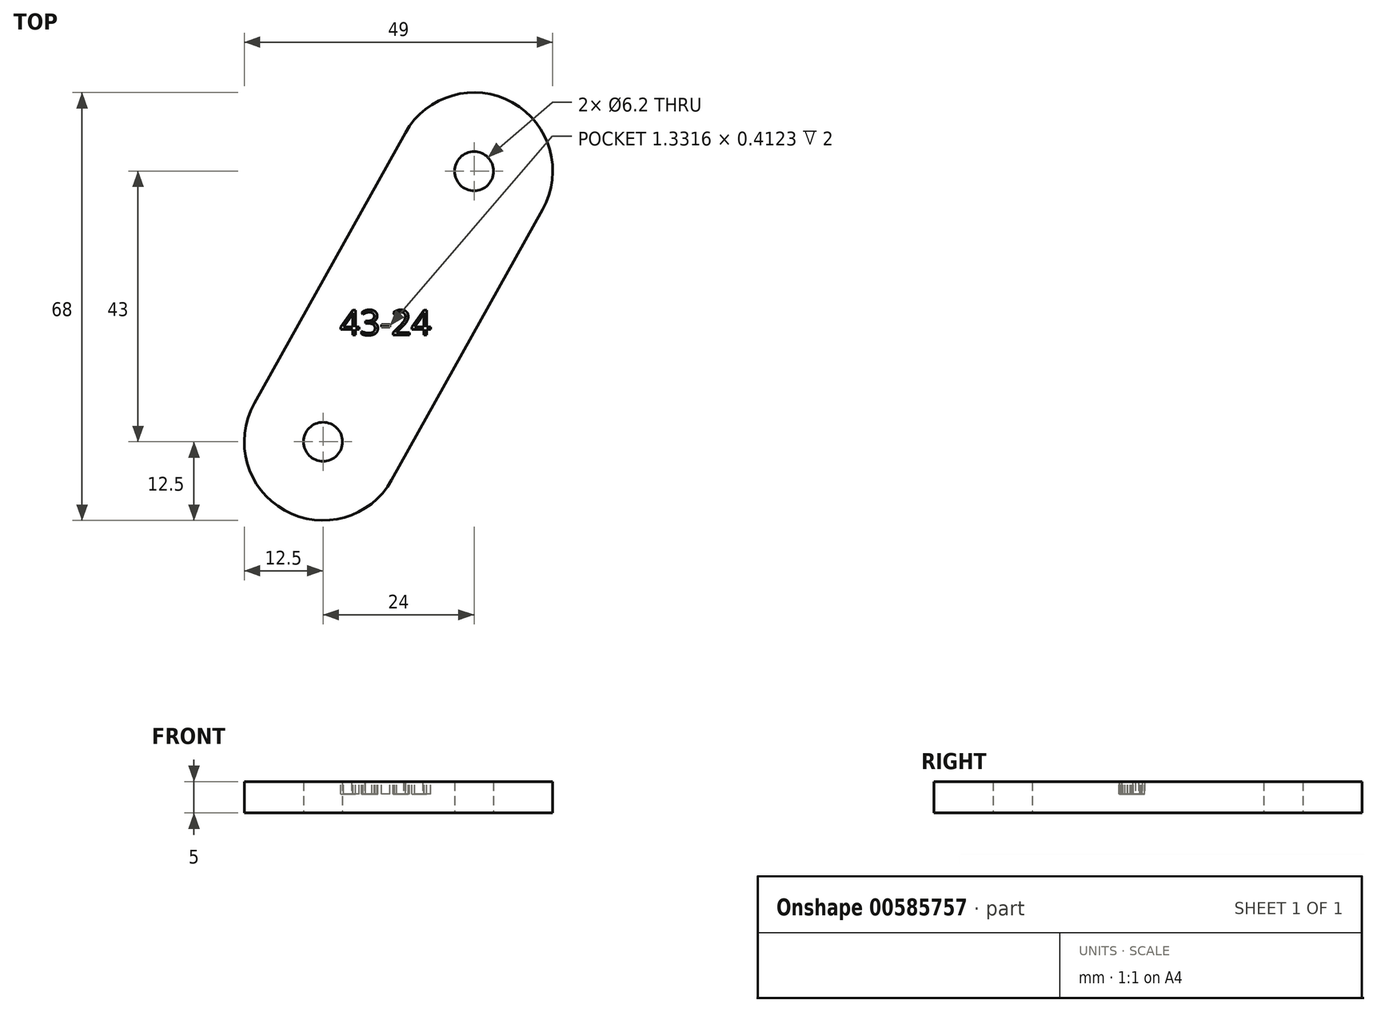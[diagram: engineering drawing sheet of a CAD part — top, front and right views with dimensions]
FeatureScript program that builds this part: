
annotation { "Feature Type Name" : "Feature", "Feature Type Description" : "" }
export const myFeature = defineFeature(function(context is Context, id is Id, definition is map)
    precondition{}
    {
        {
            assignVariable(context, id + "F0", {"name" : "Epaisseur", "anyValue" : 5});
        }
        {
            var Q0;
            Q0=qCreatedBy(makeId("Top.planeOp"),FACE);
            var sketch = newSketch(context, id + "F1", { "sketchPlane" : qUnion([Q0])});
            skArc(sketch, "E0", {"start": v(-10.91, 6.1) * mm, "mid": v(-6.1, -10.91) * mm, "end": v(10.91, -6.1) * mm});
            skArc(sketch, "E1", {"start": v(34.91, 36.9) * mm, "mid": v(30.1, 53.91) * mm, "end": v(13.09, 49.1) * mm});
            skCircle(sketch, "E2", {"center": v(0, 0) * mm, "radius": 3.1 * mm});
            skCircle(sketch, "E3", {"center": v(24, 43) * mm, "radius": 3.1 * mm});
            skLineSegment(sketch, "E4", {"start": v(-10.91, 6.1) * mm, "end": v(13.09, 49.1) * mm});
            skLineSegment(sketch, "E5", {"start": v(10.91, -6.1) * mm, "end": v(34.91, 36.9) * mm});
            skSolve(sketch);
        }
        {
            var Q0;
            Q0=makeQuery(id+"F1.imprint","IMPRINT",FACE,{"disambiguationData":[TD([[makeQuery(id+"F1.imprint","IMPRINT",EDGE,{"derivedFrom":sQuery(id+"F1.wireOp",EDGE,"E0")}),1.0]])]});
            extrude(context, id + "F2", {"entities" : qUnion([Q0]), "depth" : (getVariable(context, 'Epaisseur')) * mm, "offsetDistance" : 25 * mm});
        }
        {
            var Q0;
            Q0=makeQuery(id+"F2.opExtrude","CAP_FACE",FACE,{"disambiguationData":[OSD([sQuery(id+"F1.wireOp",EDGE,"E0"),sQuery(id+"F1.wireOp",EDGE,"E1"),sQuery(id+"F1.wireOp",EDGE,"E2"),sQuery(id+"F1.wireOp",EDGE,"E3"),sQuery(id+"F1.wireOp",EDGE,"E4"),sQuery(id+"F1.wireOp",EDGE,"E5")])],"isStart":false});
            var sketch = newSketch(context, id + "F3", { "sketchPlane" : qUnion([Q0])});
            skText(sketch, "E6", { "text": "43-24", "fontName": "OpenSans-Regular.ttf"});
            const initialGuessF3  = {"E6": [0.0027, 0.01695, 1, 0, 0.004]};
            skSetInitialGuess(sketch, initialGuessF3);
            skSolve(sketch);
        }
        {
            var Q0;
            Q0 = qSketchRegion(id + "F3", true);
            extrude(context, id + "F4", {"entities" : qUnion([Q0]), "operationType" : NewBodyOperationType.REMOVE, "oppositeDirection" : true, "depth" : 2 * mm, "offsetDistance" : 25 * mm});
        }
    });
